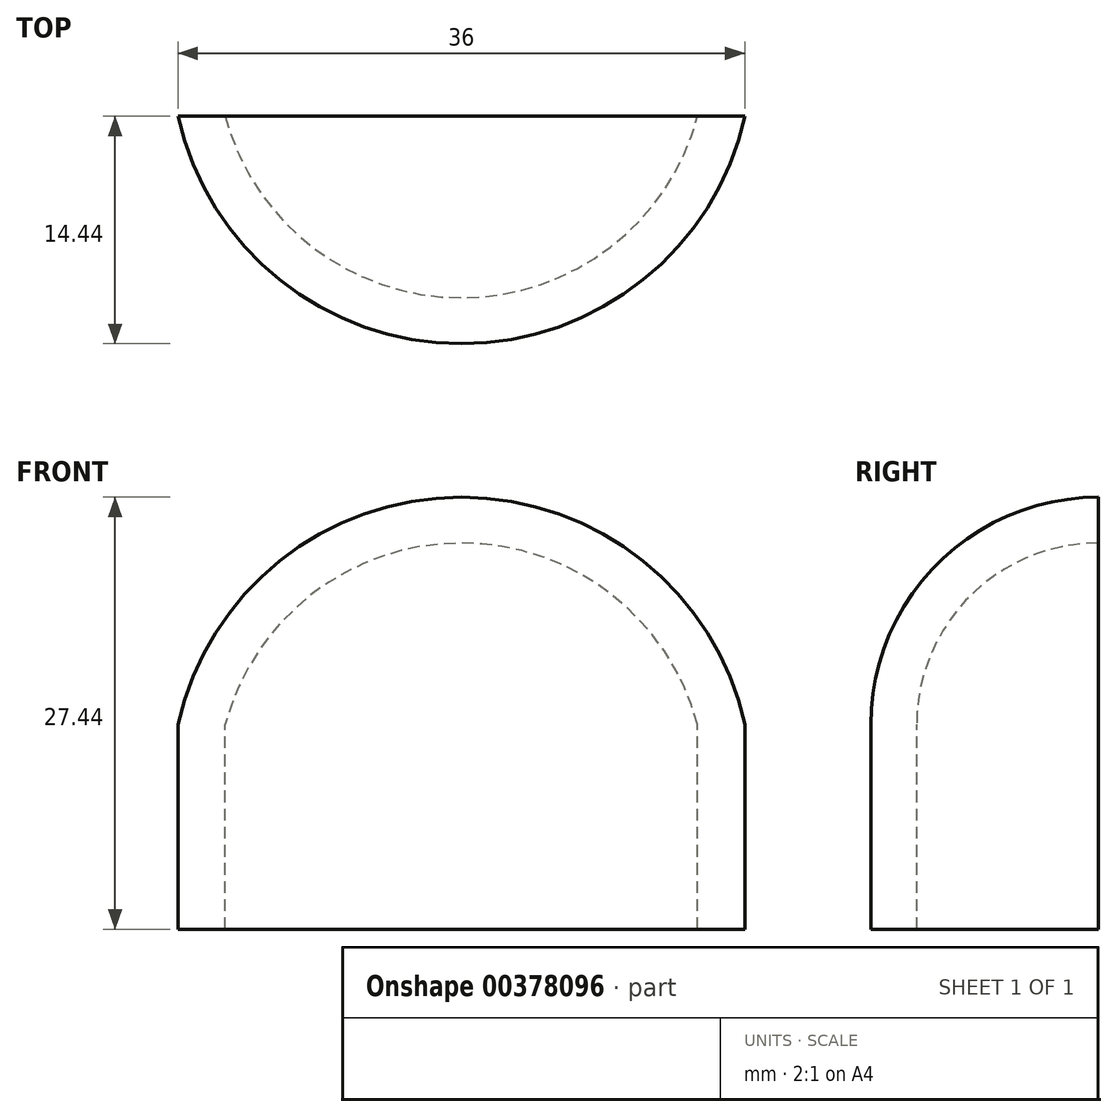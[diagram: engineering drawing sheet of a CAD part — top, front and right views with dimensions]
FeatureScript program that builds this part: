
annotation { "Feature Type Name" : "Feature", "Feature Type Description" : "" }
export const myFeature = defineFeature(function(context is Context, id is Id, definition is map)
    precondition{}
    {
        {
            var Q0;
            Q0=qCreatedBy(makeId("Top.planeOp"),FACE);
            cPlane(context, id + "F0", {"entities" : qUnion([Q0]), "cplaneType" : CPlaneType.OFFSET, "offset" : 25 * mm, "width" : 150 * mm, "height" : 150 * mm});
        }
        {
            var Q0;
            Q0=qCreatedBy(makeId("Front.planeOp"),FACE);
            var sketch = newSketch(context, id + "F1", { "sketchPlane" : qUnion([Q0])});
            skPoint(sketch, "E0", {"position": v(0, 25) * mm});
            skLineSegment(sketch, "E1", {"start": v(-18, 25) * mm, "end": v(-15, 25) * mm});
            skLineSegment(sketch, "E2.trimOffspring", {"start": v(15, 25) * mm, "end": v(18, 25) * mm});
            skLineSegment(sketch, "E3", {"start": v(0, 25) * mm, "end": v(-70.76, 25) * mm, "construction": true});
            skArc(sketch, "E4", {"start": v(15, 25) * mm, "mid": v(0, 36.52) * mm, "end": v(-15, 25) * mm});
            skArc(sketch, "E5", {"start": v(18, 25) * mm, "mid": v(0, 39.44) * mm, "end": v(-18, 25) * mm});
            skSolve(sketch);
        }
        {
            var Q0;
            Q0=makeQuery(id+"F1.imprint","IMPRINT",FACE,{"disambiguationData":[TD([[makeQuery(id+"F1.imprint","IMPRINT",EDGE,{"derivedFrom":sQuery(id+"F1.wireOp",EDGE,"E1")}),1.0]])]});
            var Q1;
            Q1=sQuery(id+"F1.wireOp",EDGE,"E3");
            revolve(context, id + "F2", {"entities" : qUnion([Q0]), "axis" : qUnion([Q1]), "revolveType" : RevolveType.ONE_DIRECTION, "oppositeDirection" : true, "angle" : 90 * degree});
        }
        {
            var Q0;
            Q0=qCreatedBy(id+"F0.planeOp",FACE);
            var sketch = newSketch(context, id + "F3", { "sketchPlane" : qUnion([Q0])});
            skPoint(sketch, "E6", {"position": v(0, 0) * mm});
            skLineSegment(sketch, "E7", {"start": v(18, 0) * mm, "end": v(15, 0) * mm});
            skLineSegment(sketch, "E8.trimOffspring", {"start": v(-15, 0) * mm, "end": v(-18, 0) * mm});
            skLineSegment(sketch, "E9", {"start": v(-117.68, 0) * mm, "end": v(0, 0) * mm, "construction": true});
            skArc(sketch, "E10", {"start": v(-18, 0) * mm, "mid": v(0, -14.44) * mm, "end": v(18, 0) * mm});
            skArc(sketch, "E11", {"start": v(-15, 0) * mm, "mid": v(0, -11.52) * mm, "end": v(15, 0) * mm});
            skSolve(sketch);
        }
        {
            var Q0;
            Q0 = qSketchRegion(id + "F3", true);
            extrude(context, id + "F4", {"entities" : qUnion([Q0]), "operationType" : NewBodyOperationType.ADD, "oppositeDirection" : true, "depth" : 13 * mm});
        }
    });
